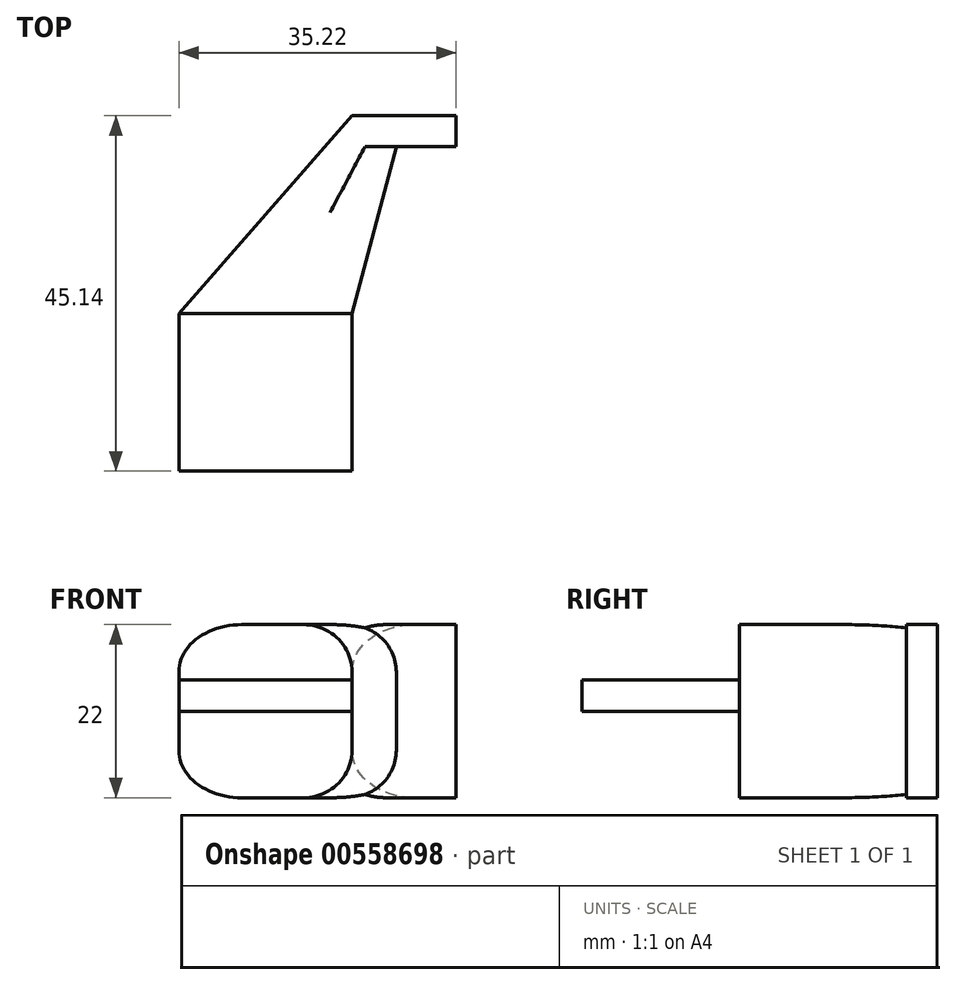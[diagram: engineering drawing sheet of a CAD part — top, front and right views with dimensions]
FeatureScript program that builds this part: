
annotation { "Feature Type Name" : "Feature", "Feature Type Description" : "" }
export const myFeature = defineFeature(function(context is Context, id is Id, definition is map)
    precondition{}
    {
        {
            var Q0;
            Q0=qCreatedBy(makeId("Top.planeOp"),FACE);
            var sketch = newSketch(context, id + "F0", { "sketchPlane" : qUnion([Q0])});
            skLineSegment(sketch, "E0.bottom", {"start": v(0, 0) * mm, "end": v(-22, 0) * mm});
            skLineSegment(sketch, "E0.top", {"start": v(0, 20) * mm, "end": v(-22, 20) * mm});
            skLineSegment(sketch, "E0.left", {"start": v(0, 0) * mm, "end": v(0, 20) * mm});
            skLineSegment(sketch, "E0.right", {"start": v(-22, 0) * mm, "end": v(-22, 20) * mm});
            skLineSegment(sketch, "E1", {"start": v(-22, 20) * mm, "end": v(0, 45.14) * mm});
            skLineSegment(sketch, "E2", {"start": v(0, 45.14) * mm, "end": v(13.22, 45.14) * mm});
            skLineSegment(sketch, "E3", {"start": v(13.22, 45.14) * mm, "end": v(13.22, 41.2) * mm});
            skLineSegment(sketch, "E4", {"start": v(13.22, 41.2) * mm, "end": v(5.63, 41.2) * mm});
            skLineSegment(sketch, "E5", {"start": v(5.63, 41.2) * mm, "end": v(0, 20) * mm});
            skSolve(sketch);
        }
        {
            var Q0;
            Q0=makeQuery(id+"F0.imprint","IMPRINT",FACE,{"disambiguationData":[TD([[makeQuery(id+"F0.imprint","IMPRINT",EDGE,{"derivedFrom":sQuery(id+"F0.wireOp",EDGE,"E0.bottom")}),-1.0]])]});
            extrude(context, id + "F1", {"entities" : qUnion([Q0]), "depth" : 4 * mm, "offsetDistance" : 25 * mm});
        }
        {
            var Q0;
            Q0=makeQuery(id+"F0.imprint","IMPRINT",FACE,{"disambiguationData":[TD([[makeQuery(id+"F0.imprint","IMPRINT",EDGE,{"derivedFrom":sQuery(id+"F0.wireOp",EDGE,"E0.top")}),-1.0]])]});
            extrude(context, id + "F2", {"entities" : qUnion([Q0]), "operationType" : NewBodyOperationType.ADD, "depth" : 11 * mm, "offsetDistance" : 25 * mm});
        }
        {
            var Q0;
            Q0=makeQuery(id+"F0.imprint","IMPRINT",FACE,{"disambiguationData":[TD([[makeQuery(id+"F0.imprint","IMPRINT",EDGE,{"derivedFrom":sQuery(id+"F0.wireOp",EDGE,"E0.top")}),-1.0]])]});
            extrude(context, id + "F3", {"entities" : qUnion([Q0]), "operationType" : NewBodyOperationType.ADD, "depth" : -11 * mm, "offsetDistance" : 25 * mm});
        }
        {
            var Q0;
            Q0=makeQuery(id+"F3.opExtrude","CAP_EDGE",EDGE,{"disambiguationData":[OSD([sQuery(id+"F0.wireOp",EDGE,"E1")])],"isStart":false});
            var Q1;
            Q1=makeQuery(id+"F2.opExtrude","CAP_EDGE",EDGE,{"disambiguationData":[OSD([sQuery(id+"F0.wireOp",EDGE,"E1")])],"isStart":false});
            var Q2;
            Q2=makeQuery(id+"F3.opExtrude","CAP_EDGE",EDGE,{"disambiguationData":[OSD([sQuery(id+"F0.wireOp",EDGE,"E5")])],"isStart":false});
            var Q3;
            Q3=makeQuery(id+"F2.opExtrude","CAP_EDGE",EDGE,{"disambiguationData":[OSD([sQuery(id+"F0.wireOp",EDGE,"E5")])],"isStart":false});
            fillet(context, id + "F4", {"entities" : qUnion([Q0, Q1, Q2, Q3]), "radius" : 6 * mm, "tangentPropagation" : true, "allowEdgeOverflow" : false});
        }
    });
